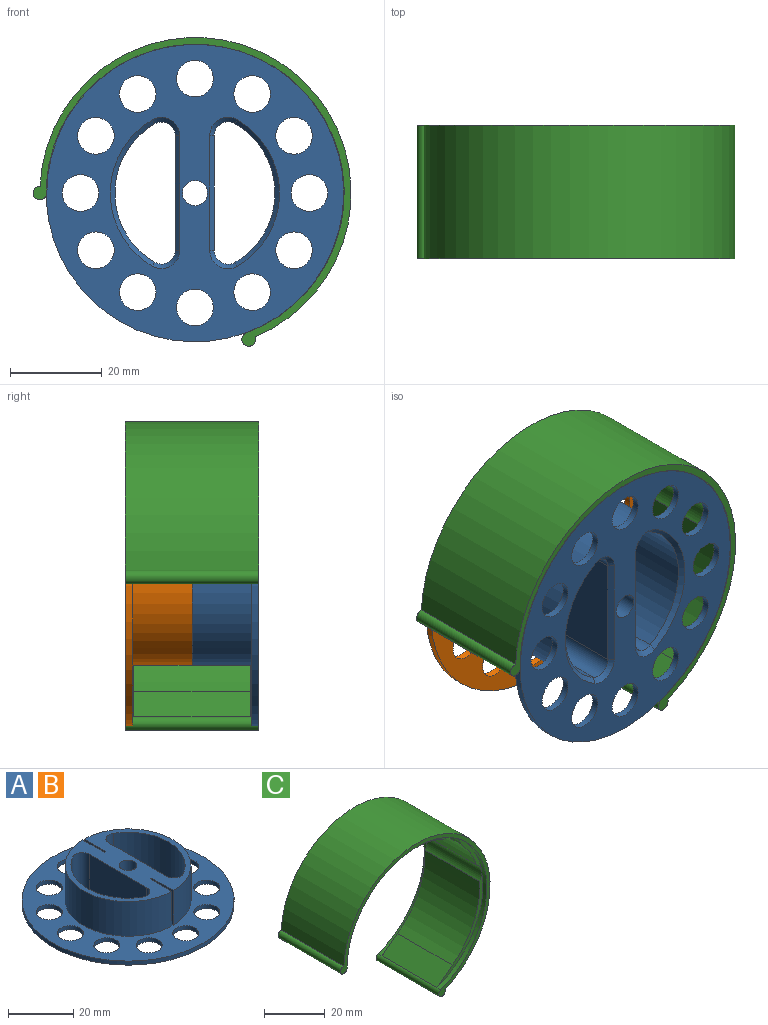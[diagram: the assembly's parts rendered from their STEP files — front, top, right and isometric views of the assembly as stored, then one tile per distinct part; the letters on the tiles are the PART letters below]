
ASSEMBLY  parts=3 mates=2
PART A: 41 faces, bbox 65x65x14.5 mm
  f0: plane 65x65mm, normal (0,0,1), area 1556.1mm2, adj f7,f8,f9,f10,f11,f12,f13,f14
  f1: cylinder r=3mm len=13.5mm, axis (0,0,-1), area 84.8mm2, adj f2,f19,f31,f38
  f2: plane 25.13x13.5mm, normal (1,0,0), area 339.2mm2, adj f1,f3,f31,f39
  f3: cylinder r=3mm len=13.5mm, axis (0,0,-1), area 84.8mm2, adj f2,f19,f31,f37
  f4: cylinder r=3mm len=13.5mm, axis (0,0,-1), area 85mm2, adj f5,f20,f31,f35
  f5: plane 25.04x13.5mm, normal (-1,0,0), area 338.1mm2, adj f4,f6,f31,f33
  f6: cylinder r=3mm len=13.5mm, axis (0,0,-1), area 85mm2, adj f5,f20,f31,f32
  f7: cylinder r=4mm len=8mm, axis (0,0,-1), area 37.7mm2, adj f0,f22
  f8: cylinder r=4mm len=8mm, axis (0,0,-1), area 37.7mm2, adj f0,f22
  f9: cylinder r=4mm len=8mm, axis (0,0,-1), area 37.7mm2, adj f0,f22
  f10: cylinder r=4mm len=8mm, axis (0,0,-1), area 37.7mm2, adj f0,f22
  f11: cylinder r=4mm len=8mm, axis (0,0,-1), area 37.7mm2, adj f0,f22
  f12: cylinder r=4mm len=8mm, axis (0,0,-1), area 37.7mm2, adj f0,f22
  f13: cylinder r=4mm len=8mm, axis (0,0,-1), area 37.7mm2, adj f0,f22
  f14: cylinder r=4mm len=8mm, axis (0,0,-1), area 37.7mm2, adj f0,f22
  f15: cylinder r=4mm len=8mm, axis (0,0,-1), area 37.7mm2, adj f0,f22
  f16: cylinder r=4mm len=8mm, axis (0,0,-1), area 37.7mm2, adj f0,f22
  f17: cylinder r=4mm len=8mm, axis (0,0,-1), area 37.7mm2, adj f0,f22
  f18: cylinder r=4mm len=8mm, axis (0,0,-1), area 37.7mm2, adj f0,f22
  f19: cylinder r=17.5mm len=30.32mm, axis (0,0,-1), area 495.1mm2, adj f1,f3,f31,f36
  f20: cylinder r=17.5mm len=30.22mm, axis (0,0,-1), area 492.5mm2, adj f4,f6,f31,f34
  f21: cylinder r=32.5mm len=65mm, axis (0,0,-1), area 306.3mm2, adj f0,f22
  f22: plane 65x65mm, normal (0,0,-1), area 1890.9mm2, adj f7,f8,f9,f10,f11,f12,f13,f14
  f23: plane 13x9.3mm, normal (1,0,0), area 120.9mm2, adj f0,f24,f30,f31
  f24: cylinder r=19.3mm len=38.6mm, axis (0,0,-1), area 780.4mm2, adj f0,f23,f25,f31
  f25: plane 13x9.3mm, normal (1,0,0), area 120.9mm2, adj f0,f24,f26,f31
  f26: plane 13x0.6mm, normal (0,-1,0), area 7.8mm2, adj f0,f25,f27,f31
  f27: plane 13x9.3mm, normal (-1,0,0), area 120.9mm2, adj f0,f26,f28,f31
  f28: cylinder r=19.3mm len=38.6mm, axis (0,0,-1), area 780.4mm2, adj f0,f27,f29,f31
  f29: plane 13x9.3mm, normal (-1,0,0), area 120.9mm2, adj f0,f28,f30,f31
  f30: plane 13x0.6mm, normal (0,1,0), area 7.8mm2, adj f0,f23,f29,f31
  f31: plane 38.6x38.6mm, normal (0,0,1), area 489.6mm2, adj f1,f2,f3,f4,f5,f6,f19,f20
  f32: cone r=4mm half-angle=45deg, axis (0,0,-1), area 10.4mm2, adj f6,f22,f33,f34
  f33: plane 25.04x1mm, normal (-0.71,0,-0.71), area 35.4mm2, adj f5,f22,f32,f35
  f34: cone r=18.5mm half-angle=45deg, axis (0,0,-1), area 53.1mm2, adj f20,f22,f32,f35
  f35: cone r=4mm half-angle=45deg, axis (0,0,-1), area 10.4mm2, adj f4,f22,f33,f34
  f36: cone r=18.5mm half-angle=45deg, axis (0,0,-1), area 53.4mm2, adj f19,f22,f37,f38
  f37: cone r=4mm half-angle=45deg, axis (0,0,-1), area 10.4mm2, adj f3,f22,f36,f39
  f38: cone r=4mm half-angle=45deg, axis (0,0,-1), area 10.4mm2, adj f1,f22,f36,f39
  f39: plane 25.13x1mm, normal (0.71,0,-0.71), area 35.5mm2, adj f2,f22,f37,f38
  f40: cylinder r=2.74mm len=14.5mm, axis (0,0,1), area 249.9mm2, adj f22,f31
PART B: same geometry as A
PART C: 22 faces, bbox 69.5x29.1x67.4 mm
  f0: cylinder r=34mm len=67.97mm, axis (0,-1,0), area 4229.8mm2, adj f11,f12,f20,f21
  f1: cylinder r=31mm len=27.3mm, axis (0,-1,0), area 801.7mm2, adj f5,f8,f18,f19
  f2: cylinder r=31mm len=26.05mm, axis (0,-1,0), area 920.1mm2, adj f6,f9,f16,f17
  f3: cylinder r=31mm len=25.5mm, axis (0,-1,0), area 281mm2, adj f7,f10,f14,f15
  f4: cylinder r=31mm len=25.5mm, axis (0,-1,0), area 355.8mm2, adj f5,f8,f14,f19
  f5: plane 56.62x21.38mm, normal (0,-1,0), area 84.7mm2, adj f1,f4,f13,f14,f18,f19
  f6: plane 32.5x32mm, normal (0,-1,0), area 66.2mm2, adj f2,f13,f16,f17
  f7: plane 18.89x6.41mm, normal (0,-1,0), area 21.3mm2, adj f3,f13,f14,f15
  f8: plane 56.62x21.38mm, normal (0,1,0), area 84.7mm2, adj f1,f4,f13,f14,f18,f19
  f9: plane 32.5x32mm, normal (0,1,0), area 66.2mm2, adj f2,f13,f16,f17
  f10: plane 18.89x6.41mm, normal (0,1,0), area 21.3mm2, adj f3,f13,f14,f15
  f11: plane 69.5x67.45mm, normal (0,1,0), area 228.3mm2, adj f0,f13,f20,f21
  f12: plane 69.5x67.45mm, normal (0,-1,0), area 228.3mm2, adj f0,f13,f20,f21
  f13: cylinder r=32.5mm len=65mm, axis (0,-1,0), area 536mm2, adj f5,f6,f7,f8,f9,f10,f11,f12
  f14: cylinder r=7.72mm len=25.5mm, axis (0,1,0), area 284mm2, adj f3,f4,f5,f7,f8,f10
  f15: cylinder r=4.74mm len=25.5mm, axis (0,1,0), area 94.3mm2, adj f3,f7,f10,f13
  f16: cylinder r=4.74mm len=25.5mm, axis (0,1,0), area 94.3mm2, adj f2,f6,f9,f13
  f17: plane 25.5x8.81mm, normal (0.95,0,-0.3), area 235.5mm2, adj f2,f6,f9,f20
  f18: plane 25.5x7.11mm, normal (-0.61,0,0.79), area 228.7mm2, adj f1,f5,f8,f21
  f19: cylinder r=5mm len=25.5mm, axis (0,1,0), area 218.3mm2, adj f1,f4,f5,f8
  f20: cylinder r=1.5mm len=29.1mm, axis (0,1,0), area 206.7mm2, adj f0,f11,f12,f13,f17
  f21: cylinder r=1.5mm len=29.1mm, axis (0,1,0), area 206.7mm2, adj f0,f11,f12,f13,f18
PLACE A rot(axis=(-1,0,0),90deg) t=(24.97,9.95,38.97)mm
PLACE B rot(axis=(1,0,0),90deg) t=(24.97,38.95,38.97)mm
PLACE C t=(25.09,4.16,38.96)mm
MATE fastened A.f28 <-> B.f28  axis (0,1,0) through (24.97,24.45,38.97)mm
MATE parallel B.f40 <-> C.f7  axis (0,-1,0) through (24.97,37.45,38.97)mm
